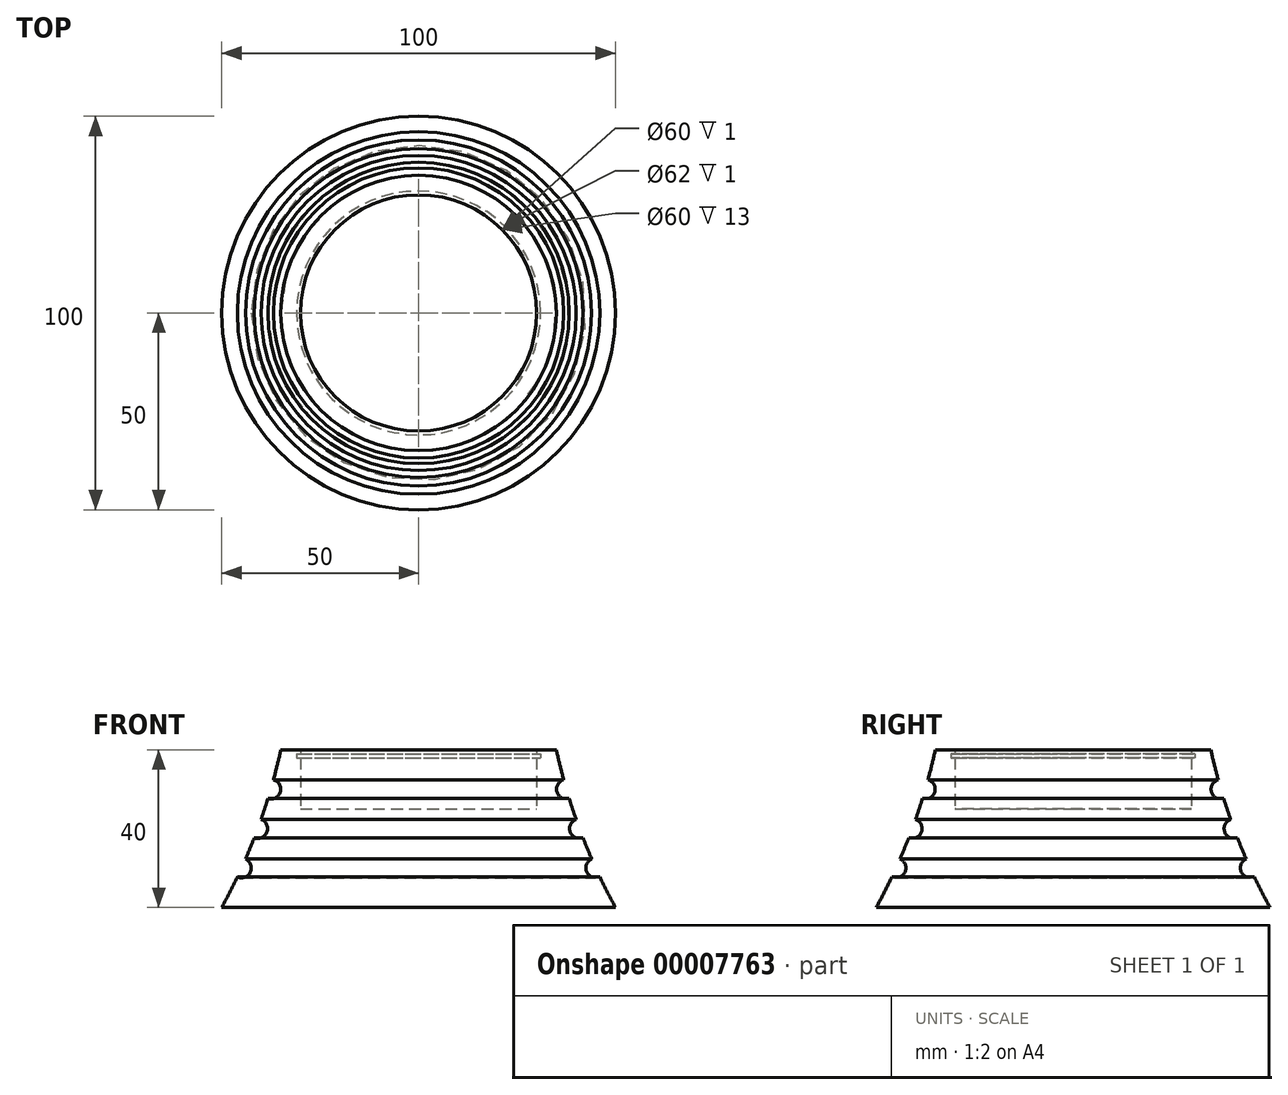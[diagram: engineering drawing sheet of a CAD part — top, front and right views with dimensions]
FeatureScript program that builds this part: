
annotation { "Feature Type Name" : "Feature", "Feature Type Description" : "" }
export const myFeature = defineFeature(function(context is Context, id is Id, definition is map)
    precondition{}
    {
        {
            var Q0;
            Q0=qCreatedBy(makeId("Front.planeOp"),FACE);
            var sketch = newSketch(context, id + "F0", { "sketchPlane" : qUnion([Q0])});
            skLineSegment(sketch, "E0", {"start": v(0, 0) * mm, "end": v(0, 25) * mm});
            skLineSegment(sketch, "E1", {"start": v(30, 40) * mm, "end": v(35, 40) * mm});
            skLineSegment(sketch, "E2", {"start": v(0, 0) * mm, "end": v(50, 0) * mm});
            skArc(sketch, "E3", {"start": v(35, 40) * mm, "mid": v(35.89, 36.2) * mm, "end": v(36.87, 32.4) * mm});
            skArc(sketch, "E4", {"start": v(36.87, 32.4) * mm, "mid": v(35.16, 29.3) * mm, "end": v(38.28, 27.6) * mm});
            skArc(sketch, "E5", {"start": v(40.02, 22.35) * mm, "mid": v(38.52, 19.13) * mm, "end": v(41.76, 17.66) * mm});
            skArc(sketch, "E6", {"start": v(43.97, 12.28) * mm, "mid": v(42.72, 8.96) * mm, "end": v(46.05, 7.73) * mm});
            skArc(sketch, "E7.trimOffspring", {"start": v(38.28, 27.6) * mm, "mid": v(39.12, 24.97) * mm, "end": v(40.02, 22.35) * mm});
            skArc(sketch, "E8.trimOffspring", {"start": v(41.76, 17.66) * mm, "mid": v(42.84, 14.96) * mm, "end": v(43.97, 12.28) * mm});
            skArc(sketch, "E9.trimOffspring", {"start": v(46.05, 7.73) * mm, "mid": v(47.97, 3.84) * mm, "end": v(50, 0) * mm});
            skLineSegment(sketch, "E10.top", {"start": v(0, 25) * mm, "end": v(30, 25) * mm});
            skLineSegment(sketch, "E10.right", {"start": v(30, 40) * mm, "end": v(30, 39) * mm});
            skPoint(sketch, "E11.visualSharp", {"position": v(30, 40) * mm});
            skLineSegment(sketch, "E12.bottom", {"start": v(30, 39) * mm, "end": v(31, 39) * mm});
            skLineSegment(sketch, "E12.top", {"start": v(30, 38) * mm, "end": v(31, 38) * mm});
            skLineSegment(sketch, "E12.right", {"start": v(31, 39) * mm, "end": v(31, 38) * mm});
            skLineSegment(sketch, "E13.trimOffspring", {"start": v(30, 38) * mm, "end": v(30, 25) * mm});
            skSolve(sketch);
        }
        {
            var Q0;
            Q0 = qSketchRegion(id + "F0", true);
            var Q1;
            Q1=sQuery(id+"F0.wireOp",EDGE,"E0");
            revolve(context, id + "F1", {"entities" : qUnion([Q0]), "axis" : qUnion([Q1]), "revolveType" : RevolveType.ONE_DIRECTION, "angle" : 360 * degree});
        }
    });
